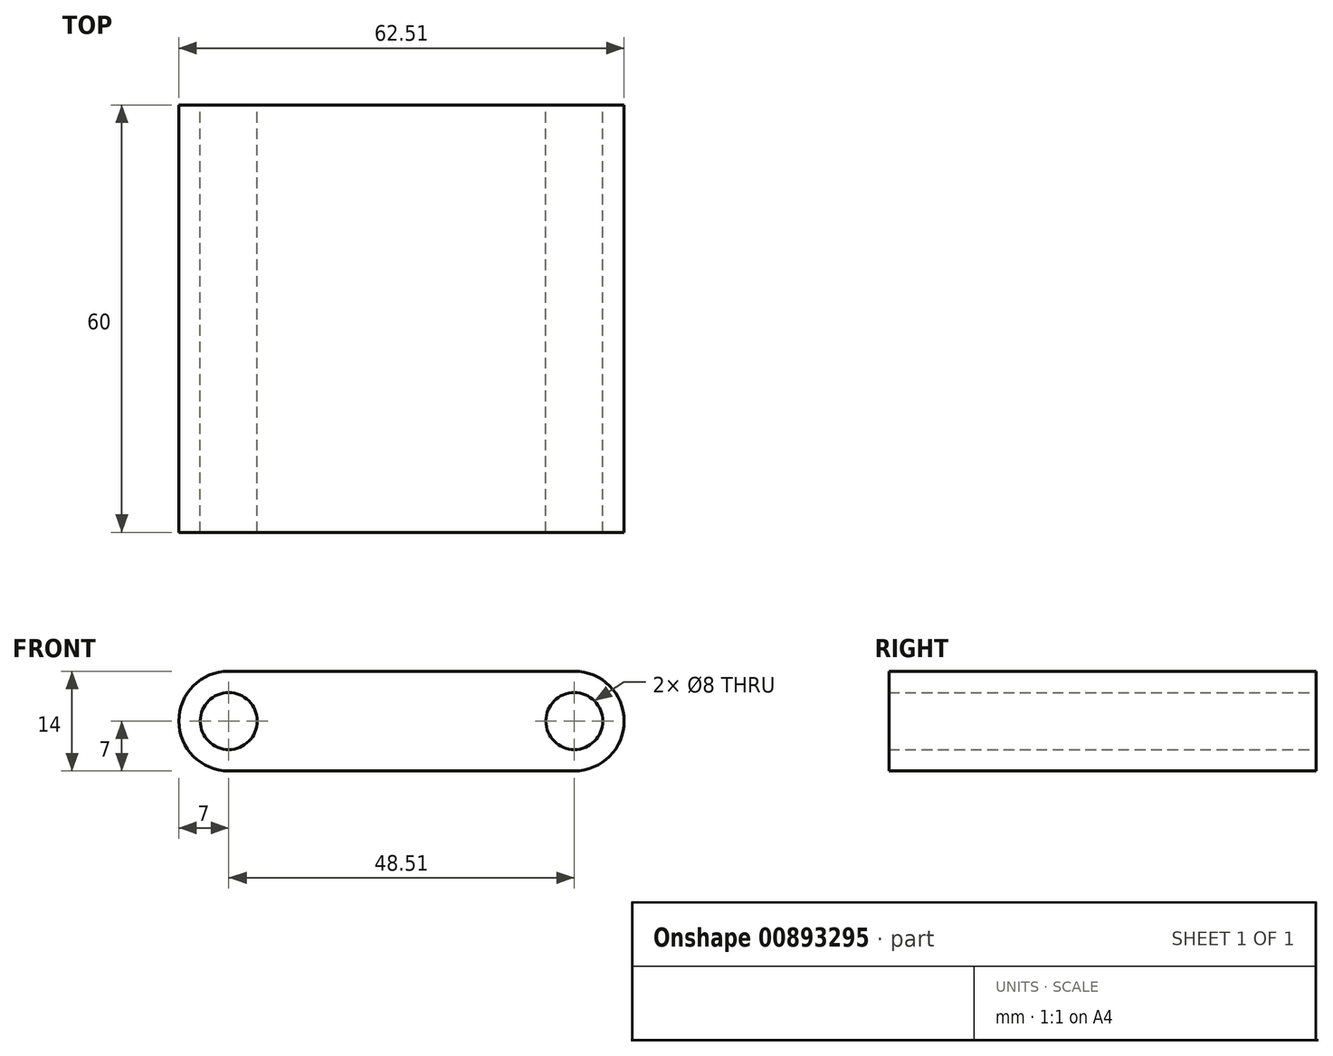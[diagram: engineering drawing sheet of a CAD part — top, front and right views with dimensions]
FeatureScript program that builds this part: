
annotation { "Feature Type Name" : "Feature", "Feature Type Description" : "" }
export const myFeature = defineFeature(function(context is Context, id is Id, definition is map)
    precondition{}
    {
        {
            assignVariable(context, id + "F0", {"name" : "Thickness", "anyValue" : 60});
        }
        {
            var Q0;
            Q0=qCreatedBy(makeId("Front.planeOp"),FACE);
            var sketch = newSketch(context, id + "F1", { "sketchPlane" : qUnion([Q0])});
            skCircle(sketch, "E0", {"center": v(0, 0) * mm, "radius": 4 * mm});
            skCircle(sketch, "E1", {"center": v(48.5, 0) * mm, "radius": 4 * mm});
            skArc(sketch, "E2", {"start": v(48.5, -7) * mm, "mid": v(55.5, 0) * mm, "end": v(48.5, 7) * mm});
            skArc(sketch, "E3", {"start": v(0, 7) * mm, "mid": v(-7, 0) * mm, "end": v(0, -7) * mm});
            skLineSegment(sketch, "E4", {"start": v(0, 7) * mm, "end": v(48.5, 7) * mm});
            skLineSegment(sketch, "E5", {"start": v(0, -7) * mm, "end": v(48.5, -7) * mm});
            skSolve(sketch);
        }
        {
            var Q0;
            Q0=makeQuery(id+"F1.imprint","IMPRINT",FACE,{"disambiguationData":[TD([[makeQuery(id+"F1.imprint","IMPRINT",EDGE,{"derivedFrom":sQuery(id+"F1.wireOp",EDGE,"E0")}),-1.0]])]});
            extrude(context, id + "F2", {"entities" : qUnion([Q0]), "depth" : (getVariable(context, 'Thickness')) * mm, "offsetDistance" : 25 * mm});
        }
    });
